# Revit family: Boiler filling and draining valve 2512 11
name_source: partatom
category: Rohrzubehör
revit_build: Autodesk Revit 2018 (Build: 20190510_1515(x64)
units: mm (PartAtom-declared; Revit-internal decimal feet)

## family parameters
Arbeitsebenenbasiert = Nein
Beim Laden mit Abzugskörper schneiden = Nein
Bemaßung runder Anschluss = Durchmesser verwenden
Gemeinsam genutzt = Nein
Immer vertikal = Ja
OmniClass-Nummer = 23.65.55.14
OmniClass-Titel = Valves for Liquid Services
Teiletyp = Normal

## types (1)
- Boiler filling and draining valve 2512 11
    Application = the drain valves are installed as valves to fill and drain systems.
fields of application are building services, such as in heating or chilled water plant in buildings.
aromatic chlorinated hydrocarbons such as natural gas or petroleum occurring in, destroy the EPDM seals.
    Ball = forged brass CW617N, full bore, surface chrome plated
    Body = forged brass CW617N
    D02 = 9.3 mm  [stored 0.0305118 ft]
    D03 = 11.7 mm  [stored 0.0383858 ft]
    D04 = 11.1 mm  [stored 0.0364173 ft]
    D05 = 13.4 mm  [stored 0.0439633 ft]
    D06 = 12.1 mm
    D07 = 14.5 mm  [stored 0.0475722 ft]
    D08 = 7 mm  [stored 0.0229659 ft]
    G02 = 13.2 mm  [stored 0.0433071 ft]
    H00 = 17 mm
    Hersteller = Herz-Armaturen GmbH
    L00 = 44 mm  [stored 0.144357 ft]
    L01 = 19.5 mm  [stored 0.0639764 ft]
    L02 = 13 mm
    L03 = 8.5 mm  [stored 0.0278871 ft]
    L04 = 9.5 mm  [stored 0.031168 ft]
    L05 = 6.5 mm
    L06 = 19 mm  [stored 0.062336 ft]
    L07 = 4 mm  [stored 0.0131234 ft]
    L08 = 8 mm  [stored 0.0262467 ft]
    L09 = 13.5 mm  [stored 0.0442913 ft]
    L10 = 14 mm  [stored 0.0459318 ft]
    Medium = heating water according ÖNORM H5195 or VDI-Standard 2035.
the use of ethylene, or propylene glycol in a mixing ratio 25-50% is allowed.
    R01 = 7 mm  [stored 0.0229659 ft]
    R99 = 2 mm  [stored 0.00656168 ft]
    S01 = 51 mm  [stored 0.167323 ft]
    S02 = 24.5 mm
    S03 = 16 mm  [stored 0.0524934 ft]
    S04 = 45 mm  [stored 0.147638 ft]
    SCRNCODE = 05;08;01
    SCRNSEQ = ARM;ARM_TYP="ABSV";1
    SCTWCODE = 01;10;01
    SCTWSEQ = ENT;AO;1
    Sealings = ball: PTFE; spindle: PTFE
    Spindle = brass CW614N
    URL = www.herzvalves.com
    max. Operating pressure = 1000000.0 Pa
    max. Operating temperature = 110 °C
    min. Operating temperature = -30 °C

note: [stored X ft] marks values corroborated as IEEE doubles in the binary element streams (Revit-internal decimal feet)
